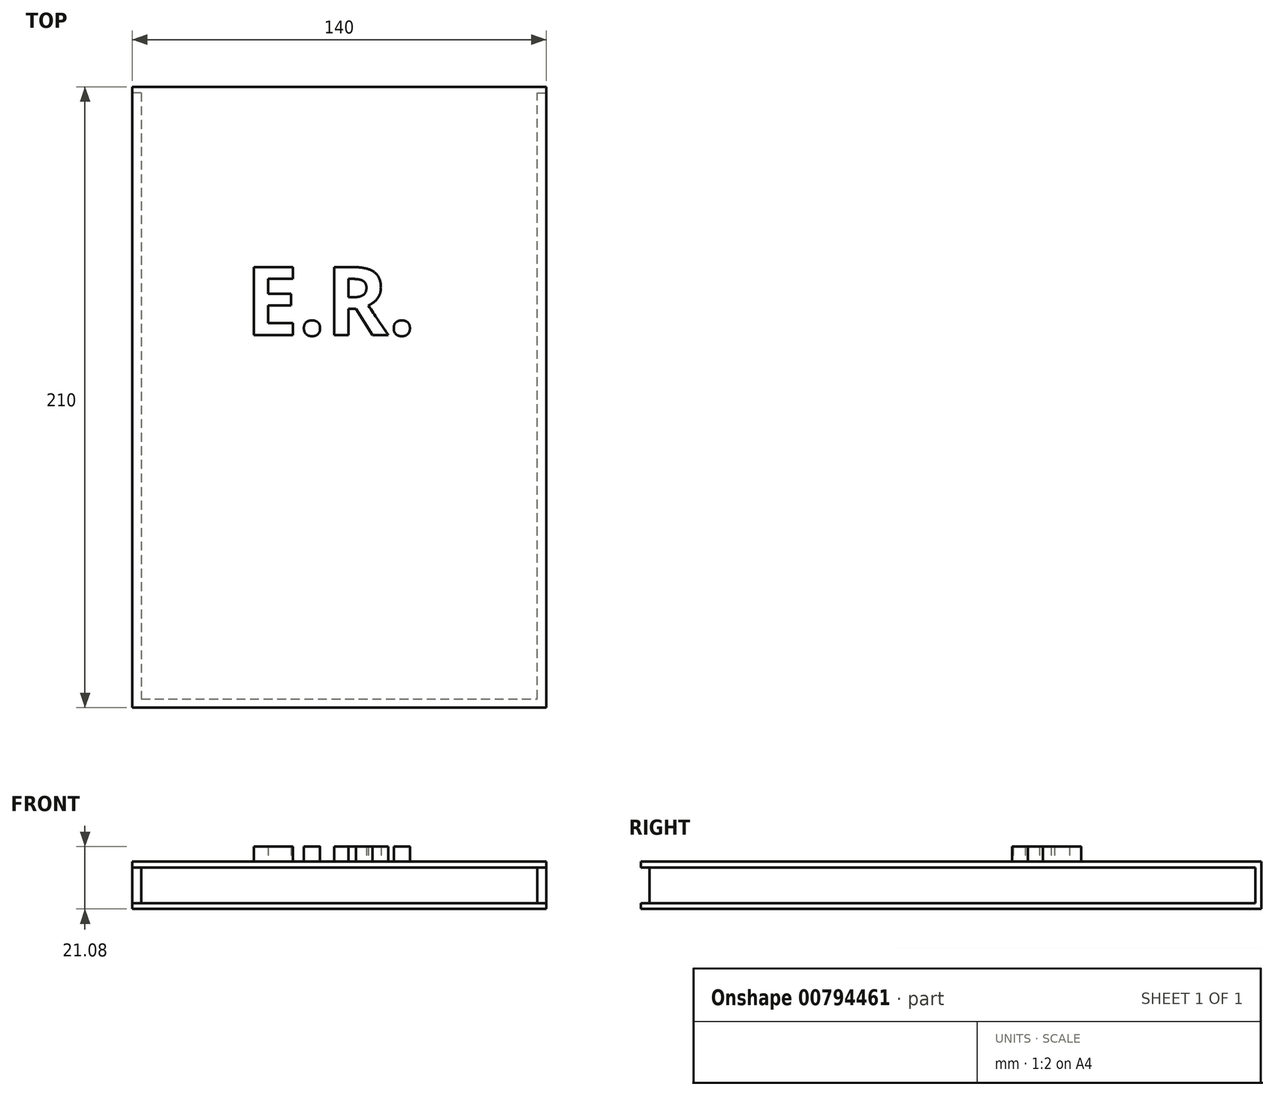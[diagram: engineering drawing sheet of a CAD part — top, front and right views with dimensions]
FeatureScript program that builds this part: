
annotation { "Feature Type Name" : "Feature", "Feature Type Description" : "" }
export const myFeature = defineFeature(function(context is Context, id is Id, definition is map)
    precondition{}
    {
        {
            var Q0;
            Q0=qCreatedBy(makeId("Top.planeOp"),FACE);
            var sketch = newSketch(context, id + "F0", { "sketchPlane" : qUnion([Q0])});
            skLineSegment(sketch, "E0.bottom", {"start": v(-63.56, 83.93) * mm, "end": v(76.44, 83.93) * mm});
            skLineSegment(sketch, "E0.top", {"start": v(-63.56, -126.07) * mm, "end": v(76.44, -126.07) * mm});
            skLineSegment(sketch, "E0.left", {"start": v(-63.56, 83.93) * mm, "end": v(-63.56, -126.07) * mm});
            skLineSegment(sketch, "E0.right", {"start": v(76.44, 83.93) * mm, "end": v(76.44, -126.07) * mm});
            skSolve(sketch);
        }
        {
            var Q0;
            Q0 = qSketchRegion(id + "F0", true);
            extrude(context, id + "F1", {"entities" : qUnion([Q0]), "depth" : 16 * mm, "offsetDistance" : 25.4 * mm});
        }
        {
            var Q0;
            Q0=makeQuery(id+"F1.opExtrude","SWEPT_FACE",FACE,{"disambiguationData":[OSD([sQuery(id+"F0.wireOp",EDGE,"E0.right")])]});
            var sketch = newSketch(context, id + "F2", { "sketchPlane" : qUnion([Q0])});
            skLineSegment(sketch, "E1.bottom", {"start": v(-126.07, 14) * mm, "end": v(81.93, 14) * mm});
            skLineSegment(sketch, "E1.top", {"start": v(-126.07, 2) * mm, "end": v(81.93, 2) * mm});
            skLineSegment(sketch, "E1.left", {"start": v(-126.07, 14) * mm, "end": v(-126.07, 2) * mm});
            skLineSegment(sketch, "E1.right", {"start": v(81.93, 14) * mm, "end": v(81.93, 2) * mm});
            skSolve(sketch);
        }
        {
            var Q0;
            Q0=makeQuery(id+"F1.opExtrude","SWEPT_FACE",FACE,{"disambiguationData":[OSD([sQuery(id+"F0.wireOp",EDGE,"E0.left")])]});
            var sketch = newSketch(context, id + "F3", { "sketchPlane" : qUnion([Q0])});
            skLineSegment(sketch, "E2.bottom", {"start": v(-81.93, 14) * mm, "end": v(126.07, 14) * mm});
            skLineSegment(sketch, "E2.top", {"start": v(-81.93, 2) * mm, "end": v(126.07, 2) * mm});
            skLineSegment(sketch, "E2.left", {"start": v(-81.93, 14) * mm, "end": v(-81.93, 2) * mm});
            skLineSegment(sketch, "E2.right", {"start": v(126.07, 14) * mm, "end": v(126.07, 2) * mm});
            skSolve(sketch);
        }
        {
            var Q0;
            Q0=makeQuery(id+"F1.opExtrude","SWEPT_FACE",FACE,{"disambiguationData":[OSD([sQuery(id+"F0.wireOp",EDGE,"E0.top")])]});
            var sketch = newSketch(context, id + "F4", { "sketchPlane" : qUnion([Q0])});
            skLineSegment(sketch, "E3.bottom", {"start": v(-63.56, 14) * mm, "end": v(76.44, 14) * mm});
            skLineSegment(sketch, "E3.top", {"start": v(-63.56, 2) * mm, "end": v(76.44, 2) * mm});
            skLineSegment(sketch, "E3.left", {"start": v(-63.56, 14) * mm, "end": v(-63.56, 2) * mm});
            skLineSegment(sketch, "E3.right", {"start": v(76.44, 14) * mm, "end": v(76.44, 2) * mm});
            skSolve(sketch);
        }
        {
            var Q0;
            Q0=makeQuery(id+"F2.imprint","IMPRINT",FACE,{"disambiguationData":[TD([[makeQuery(id+"F2.imprint","IMPRINT",EDGE,{"derivedFrom":sQuery(id+"F2.wireOp",EDGE,"E1.bottom")}),-1.0]])]});
            extrude(context, id + "F5", {"entities" : qUnion([Q0]), "operationType" : NewBodyOperationType.REMOVE, "oppositeDirection" : true, "depth" : 3 * mm, "offsetDistance" : 25 * mm});
        }
        {
            var Q0;
            Q0=makeQuery(id+"F4.imprint","IMPRINT",FACE,{"disambiguationData":[TD([[makeQuery(id+"F4.imprint","IMPRINT",EDGE,{"derivedFrom":sQuery(id+"F4.wireOp",EDGE,"E3.bottom")}),-1.0]])]});
            extrude(context, id + "F6", {"entities" : qUnion([Q0]), "operationType" : NewBodyOperationType.REMOVE, "oppositeDirection" : true, "depth" : 3 * mm, "offsetDistance" : 25 * mm});
        }
        {
            var Q0;
            Q0=makeQuery(id+"F3.imprint","IMPRINT",FACE,{"disambiguationData":[TD([[makeQuery(id+"F3.imprint","IMPRINT",EDGE,{"derivedFrom":sQuery(id+"F3.wireOp",EDGE,"E2.bottom")}),-1.0]])]});
            extrude(context, id + "F7", {"entities" : qUnion([Q0]), "operationType" : NewBodyOperationType.REMOVE, "oppositeDirection" : true, "depth" : 3 * mm, "offsetDistance" : 25 * mm});
        }
        {
            var Q0;
            Q0=makeQuery(id+"F1.opExtrude","CAP_FACE",FACE,{"disambiguationData":[OSD([sQuery(id+"F0.wireOp",EDGE,"E0.bottom"),sQuery(id+"F0.wireOp",EDGE,"E0.top"),sQuery(id+"F0.wireOp",EDGE,"E0.left"),sQuery(id+"F0.wireOp",EDGE,"E0.right")])],"isStart":false});
            var sketch = newSketch(context, id + "F8", { "sketchPlane" : qUnion([Q0])});
            skText(sketch, "E4", { "text": "E.R.\n", "fontName": "OpenSans-Bold.ttf"});
            const initialGuessF8  = {"E4": [-0.02536, 0, 1, 0, 0.02314]};
            skSetInitialGuess(sketch, initialGuessF8);
            skSolve(sketch);
        }
        {
            var Q0;
            Q0 = qSketchRegion(id + "F8", true);
            extrude(context, id + "F9", {"entities" : qUnion([Q0]), "operationType" : NewBodyOperationType.ADD, "depth" : 5.08 * mm, "offsetDistance" : 25 * mm});
        }
    });
